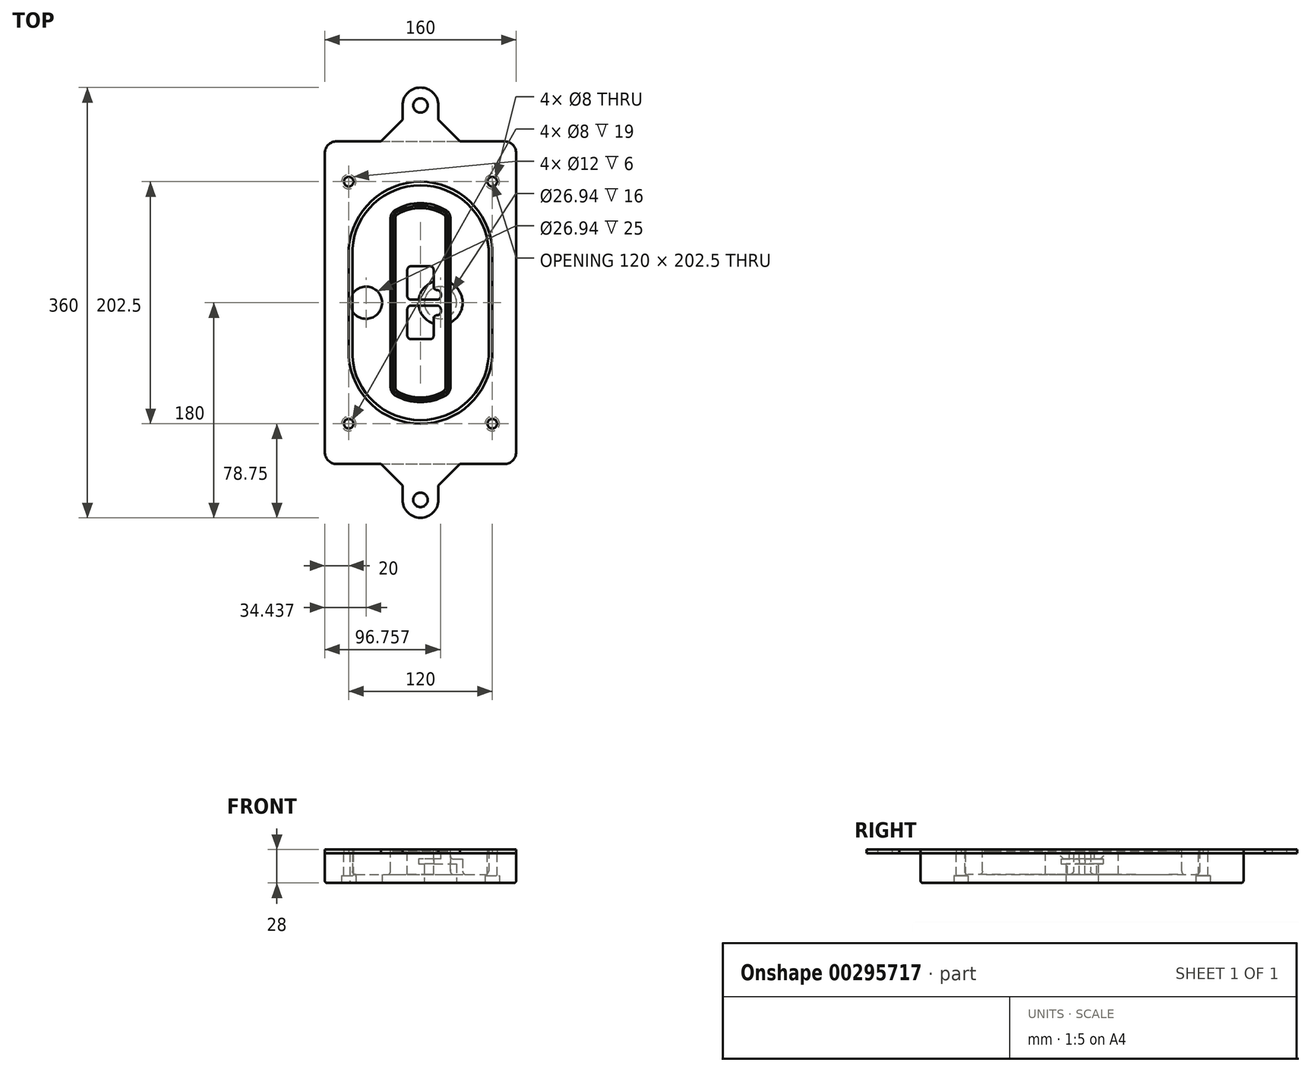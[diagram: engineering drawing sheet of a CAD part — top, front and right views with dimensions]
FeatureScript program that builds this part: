
annotation { "Feature Type Name" : "Feature", "Feature Type Description" : "" }
export const myFeature = defineFeature(function(context is Context, id is Id, definition is map)
    precondition{}
    {
        {
            var Q0;
            Q0=qCreatedBy(makeId("Top.planeOp"),FACE);
            var sketch = newSketch(context, id + "F0", { "sketchPlane" : qUnion([Q0])});
            skPoint(sketch, "E0.rect.middle", {"position": v(0, 0) * mm});
            skLineSegment(sketch, "E1.bottom", {"start": v(-70, -135) * mm, "end": v(70, -135) * mm});
            skLineSegment(sketch, "E1.top", {"start": v(-70, 135) * mm, "end": v(70, 135) * mm});
            skLineSegment(sketch, "E1.left", {"start": v(-80, -125) * mm, "end": v(-80, 125) * mm});
            skLineSegment(sketch, "E1.right", {"start": v(80, -125) * mm, "end": v(80, 125) * mm});
            skLineSegment(sketch, "E2", {"start": v(-80, 135) * mm, "end": v(80, -135) * mm, "construction": true});
            skLineSegment(sketch, "E3", {"start": v(80, 135) * mm, "end": v(-80, -135) * mm, "construction": true});
            skCircle(sketch, "E4", {"center": v(-60, 101.25) * mm, "radius": 4 * mm});
            skCircle(sketch, "E5", {"center": v(60, 101.25) * mm, "radius": 4 * mm});
            skCircle(sketch, "E6", {"center": v(60, -101.25) * mm, "radius": 4 * mm});
            skCircle(sketch, "E7", {"center": v(-60, -101.25) * mm, "radius": 4 * mm});
            skLineSegment(sketch, "E8", {"start": v(-60, 101.25) * mm, "end": v(60, 101.25) * mm, "construction": true});
            skLineSegment(sketch, "E9", {"start": v(60, 101.25) * mm, "end": v(60, -101.25) * mm, "construction": true});
            skLineSegment(sketch, "E10", {"start": v(60, -101.25) * mm, "end": v(-60, -101.25) * mm, "construction": true});
            skLineSegment(sketch, "E11", {"start": v(-60, -101.25) * mm, "end": v(-60, 101.25) * mm, "construction": true});
            skLineSegment(sketch, "E12", {"start": v(-60, 44.66) * mm, "end": v(-60, -44.66) * mm});
            skLineSegment(sketch, "E13", {"start": v(60, 44.66) * mm, "end": v(60, -44.66) * mm});
            skArc(sketch, "E14", {"start": v(59.98, 45.37) * mm, "mid": v(0, 101.25) * mm, "end": v(-59.98, 45.37) * mm});
            skArc(sketch, "E15", {"start": v(-59.98, -45.37) * mm, "mid": v(0, -101.25) * mm, "end": v(59.98, -45.37) * mm});
            skLineSegment(sketch, "E16", {"start": v(-60, 0) * mm, "end": v(60, 0) * mm, "construction": true});
            skPoint(sketch, "E17.visualSharp", {"position": v(-60, -45) * mm});
            skArc(sketch, "E17.filletArc", {"start": v(-60, -44.66) * mm, "mid": v(-60, -45.02) * mm, "end": v(-59.98, -45.37) * mm});
            skPoint(sketch, "E18.visualSharp", {"position": v(-60, 45) * mm});
            skArc(sketch, "E18.filletArc", {"start": v(-59.98, 45.37) * mm, "mid": v(-60, 45.02) * mm, "end": v(-60, 44.66) * mm});
            skPoint(sketch, "E19.visualSharp", {"position": v(60, 45) * mm});
            skArc(sketch, "E19.filletArc", {"start": v(60, 44.66) * mm, "mid": v(60, 45.02) * mm, "end": v(59.98, 45.37) * mm});
            skPoint(sketch, "E20.visualSharp", {"position": v(60, -45) * mm});
            skArc(sketch, "E20.filletArc", {"start": v(59.98, -45.37) * mm, "mid": v(60, -45.02) * mm, "end": v(60, -44.66) * mm});
            skPoint(sketch, "E21.visualSharp", {"position": v(-80, 135) * mm});
            skArc(sketch, "E21.filletArc", {"start": v(-70, 135) * mm, "mid": v(-77.07, 132.07) * mm, "end": v(-80, 125) * mm});
            skPoint(sketch, "E22.visualSharp", {"position": v(80, 135) * mm});
            skArc(sketch, "E22.filletArc", {"start": v(80, 125) * mm, "mid": v(77.07, 132.07) * mm, "end": v(70, 135) * mm});
            skPoint(sketch, "E23.visualSharp", {"position": v(80, -135) * mm});
            skArc(sketch, "E23.filletArc", {"start": v(70, -135) * mm, "mid": v(77.07, -132.07) * mm, "end": v(80, -125) * mm});
            skPoint(sketch, "E24.visualSharp", {"position": v(-80, -135) * mm});
            skArc(sketch, "E24.filletArc", {"start": v(-80, -125) * mm, "mid": v(-77.07, -132.07) * mm, "end": v(-70, -135) * mm});
            skArc(sketch, "E25.0", {"start": v(57, 44.66) * mm, "mid": v(57, 44.9) * mm, "end": v(56.98, 45.16) * mm});
            skLineSegment(sketch, "E25.1", {"start": v(57, 44.66) * mm, "end": v(57, -44.66) * mm});
            skArc(sketch, "E25.2", {"start": v(56.98, -45.16) * mm, "mid": v(57, -44.9) * mm, "end": v(57, -44.66) * mm});
            skArc(sketch, "E25.3", {"start": v(-56.98, -45.16) * mm, "mid": v(0, -98.25) * mm, "end": v(56.98, -45.16) * mm});
            skArc(sketch, "E25.4", {"start": v(-57, -44.66) * mm, "mid": v(-57, -44.9) * mm, "end": v(-56.98, -45.16) * mm});
            skArc(sketch, "E25.5", {"start": v(56.98, 45.16) * mm, "mid": v(0, 98.25) * mm, "end": v(-56.98, 45.16) * mm});
            skLineSegment(sketch, "E25.6", {"start": v(-57, 44.66) * mm, "end": v(-57, -44.66) * mm});
            skArc(sketch, "E25.7", {"start": v(-56.98, 45.16) * mm, "mid": v(-57, 44.9) * mm, "end": v(-57, 44.66) * mm});
            skArc(sketch, "E26.0", {"start": v(-63.97, 45.65) * mm, "mid": v(-64, 45.16) * mm, "end": v(-64, 44.66) * mm});
            skArc(sketch, "E26.1", {"start": v(63.97, 45.65) * mm, "mid": v(0, 105.25) * mm, "end": v(-63.97, 45.65) * mm});
            skArc(sketch, "E26.2", {"start": v(64, 44.66) * mm, "mid": v(64, 45.16) * mm, "end": v(63.97, 45.65) * mm});
            skLineSegment(sketch, "E26.3", {"start": v(64, 44.66) * mm, "end": v(64, -44.66) * mm});
            skArc(sketch, "E26.4", {"start": v(63.97, -45.65) * mm, "mid": v(64, -45.16) * mm, "end": v(64, -44.66) * mm});
            skLineSegment(sketch, "E26.5", {"start": v(-64, 44.66) * mm, "end": v(-64, -44.66) * mm});
            skArc(sketch, "E26.6", {"start": v(-63.97, -45.65) * mm, "mid": v(0, -105.25) * mm, "end": v(63.97, -45.65) * mm});
            skArc(sketch, "E26.7", {"start": v(-64, -44.66) * mm, "mid": v(-64, -45.16) * mm, "end": v(-63.97, -45.65) * mm});
            skSolve(sketch);
        }
        {
            var Q0;
            Q0=makeQuery(id+"F0.imprint","IMPRINT",FACE,{"disambiguationData":[TD([[makeQuery(id+"F0.imprint","IMPRINT",EDGE,{"derivedFrom":sQuery(id+"F0.wireOp",EDGE,"E1.bottom")}),1.0]])]});
            var Q1;
            Q1=makeQuery(id+"F0.imprint","IMPRINT",FACE,{"disambiguationData":[TD([[makeQuery(id+"F0.imprint","IMPRINT",EDGE,{"derivedFrom":sQuery(id+"F0.wireOp",EDGE,"E12")}),1.0]])]});
            var Q2;
            Q2=makeQuery(id+"F0.imprint","IMPRINT",FACE,{"disambiguationData":[TD([[makeQuery(id+"F0.imprint","IMPRINT",EDGE,{"derivedFrom":sQuery(id+"F0.wireOp",EDGE,"E25.0")}),1.0]])]});
            var Q3;
            Q3=makeQuery(id+"F0.imprint","IMPRINT",FACE,{"disambiguationData":[TD([[makeQuery(id+"F0.imprint","IMPRINT",EDGE,{"derivedFrom":sQuery(id+"F0.wireOp",EDGE,"E12")}),-1.0]])]});
            extrude(context, id + "F1", {"entities" : qUnion([Q0, Q1, Q2, Q3]), "oppositeDirection" : true, "depth" : 25 * mm});
        }
        {
            var Q0;
            Q0=makeQuery(id+"F0.imprint","IMPRINT",FACE,{"disambiguationData":[TD([[makeQuery(id+"F0.imprint","IMPRINT",EDGE,{"derivedFrom":sQuery(id+"F0.wireOp",EDGE,"E12")}),1.0]])]});
            extrude(context, id + "F2", {"entities" : qUnion([Q0]), "operationType" : NewBodyOperationType.ADD, "depth" : 3 * mm});
        }
        {
            var Q0;
            Q0=makeQuery(id+"F0.imprint","IMPRINT",FACE,{"disambiguationData":[TD([[makeQuery(id+"F0.imprint","IMPRINT",EDGE,{"derivedFrom":sQuery(id+"F0.wireOp",EDGE,"E25.0")}),1.0]])]});
            extrude(context, id + "F3", {"entities" : qUnion([Q0]), "operationType" : NewBodyOperationType.REMOVE, "oppositeDirection" : true, "depth" : 18 * mm});
        }
        {
            var Q0;
            Q0=makeQuery(id+"F2.opExtrude","CAP_FACE",FACE,{"disambiguationData":[OSD([sQuery(id+"F0.wireOp",EDGE,"E12"),sQuery(id+"F0.wireOp",EDGE,"E13"),sQuery(id+"F0.wireOp",EDGE,"E14"),sQuery(id+"F0.wireOp",EDGE,"E15"),sQuery(id+"F0.wireOp",EDGE,"E17.filletArc"),sQuery(id+"F0.wireOp",EDGE,"E18.filletArc"),sQuery(id+"F0.wireOp",EDGE,"E19.filletArc"),sQuery(id+"F0.wireOp",EDGE,"E20.filletArc"),sQuery(id+"F0.wireOp",EDGE,"E25.0"),sQuery(id+"F0.wireOp",EDGE,"E25.1"),sQuery(id+"F0.wireOp",EDGE,"E25.2"),sQuery(id+"F0.wireOp",EDGE,"E25.3"),sQuery(id+"F0.wireOp",EDGE,"E25.4"),sQuery(id+"F0.wireOp",EDGE,"E25.5"),sQuery(id+"F0.wireOp",EDGE,"E25.6"),sQuery(id+"F0.wireOp",EDGE,"E25.7")])],"isStart":false});
            var sketch = newSketch(context, id + "F4", { "sketchPlane" : qUnion([Q0])});
            skArc(sketch, "E27.0", {"start": v(-20.99, -77.65) * mm, "mid": v(0, -83.25) * mm, "end": v(20.99, -77.65) * mm});
            skArc(sketch, "E28.0", {"start": v(20.99, 77.65) * mm, "mid": v(0, 83.25) * mm, "end": v(-20.99, 77.65) * mm});
            skLineSegment(sketch, "E29", {"start": v(-25, 70.71) * mm, "end": v(-25, -70.71) * mm});
            skLineSegment(sketch, "E30", {"start": v(25, 70.71) * mm, "end": v(25, -70.71) * mm});
            skLineSegment(sketch, "E31", {"start": v(-25, 75.03) * mm, "end": v(25, 75.03) * mm, "construction": true});
            skLineSegment(sketch, "E32", {"start": v(-25, -75.03) * mm, "end": v(25, -75.03) * mm, "construction": true});
            skPoint(sketch, "E33.visualSharp", {"position": v(-25, 75.03) * mm});
            skArc(sketch, "E33.filletArc", {"start": v(-20.99, 77.65) * mm, "mid": v(-23.92, 74.72) * mm, "end": v(-25, 70.71) * mm});
            skPoint(sketch, "E34.visualSharp", {"position": v(25, 75.03) * mm});
            skArc(sketch, "E34.filletArc", {"start": v(25, 70.71) * mm, "mid": v(23.92, 74.72) * mm, "end": v(20.99, 77.65) * mm});
            skPoint(sketch, "E35.visualSharp", {"position": v(25, -75.03) * mm});
            skArc(sketch, "E35.filletArc", {"start": v(20.99, -77.65) * mm, "mid": v(23.92, -74.72) * mm, "end": v(25, -70.71) * mm});
            skPoint(sketch, "E36.visualSharp", {"position": v(-25, -75.03) * mm});
            skArc(sketch, "E36.filletArc", {"start": v(-25, -70.71) * mm, "mid": v(-23.92, -74.72) * mm, "end": v(-20.99, -77.65) * mm});
            skArc(sketch, "E37.0", {"start": v(56.98, 45.16) * mm, "mid": v(0, 98.25) * mm, "end": v(-56.98, 45.16) * mm});
            skArc(sketch, "E37.1", {"start": v(-56.98, 45.16) * mm, "mid": v(-57, 44.9) * mm, "end": v(-57, 44.66) * mm});
            skLineSegment(sketch, "E37.2", {"start": v(-57, 44.66) * mm, "end": v(-57, -44.66) * mm});
            skArc(sketch, "E37.3", {"start": v(-57, -44.66) * mm, "mid": v(-57, -44.9) * mm, "end": v(-56.98, -45.16) * mm});
            skArc(sketch, "E37.4", {"start": v(-56.98, -45.16) * mm, "mid": v(0, -98.25) * mm, "end": v(56.98, -45.16) * mm});
            skArc(sketch, "E37.5", {"start": v(56.98, -45.16) * mm, "mid": v(57, -44.9) * mm, "end": v(57, -44.66) * mm});
            skLineSegment(sketch, "E37.6", {"start": v(57, 44.66) * mm, "end": v(57, -44.66) * mm});
            skArc(sketch, "E37.7", {"start": v(57, 44.66) * mm, "mid": v(57, 44.9) * mm, "end": v(56.98, 45.16) * mm});
            skLineSegment(sketch, "E38.0", {"start": v(23, 70.71) * mm, "end": v(23, -70.71) * mm});
            skArc(sketch, "E38.1", {"start": v(19.99, -75.92) * mm, "mid": v(22.2, -73.72) * mm, "end": v(23, -70.71) * mm});
            skArc(sketch, "E38.2", {"start": v(-19.99, -75.92) * mm, "mid": v(0, -81.25) * mm, "end": v(19.99, -75.92) * mm});
            skArc(sketch, "E38.3", {"start": v(-23, -70.71) * mm, "mid": v(-22.2, -73.72) * mm, "end": v(-19.99, -75.92) * mm});
            skLineSegment(sketch, "E38.4", {"start": v(-23, 70.71) * mm, "end": v(-23, -70.71) * mm});
            skArc(sketch, "E38.5", {"start": v(23, 70.71) * mm, "mid": v(22.2, 73.72) * mm, "end": v(19.99, 75.92) * mm});
            skArc(sketch, "E38.6", {"start": v(-19.99, 75.92) * mm, "mid": v(-22.2, 73.72) * mm, "end": v(-23, 70.71) * mm});
            skArc(sketch, "E38.7", {"start": v(19.99, 75.92) * mm, "mid": v(0, 81.25) * mm, "end": v(-19.99, 75.92) * mm});
            skArc(sketch, "E39.0", {"start": v(21, 70.71) * mm, "mid": v(20.46, 72.72) * mm, "end": v(19, 74.18) * mm});
            skLineSegment(sketch, "E39.1", {"start": v(21, 70.71) * mm, "end": v(21, -70.71) * mm});
            skArc(sketch, "E39.2", {"start": v(19, -74.18) * mm, "mid": v(20.46, -72.72) * mm, "end": v(21, -70.71) * mm});
            skArc(sketch, "E39.3", {"start": v(-19, -74.18) * mm, "mid": v(0, -79.25) * mm, "end": v(19, -74.18) * mm});
            skArc(sketch, "E39.4", {"start": v(-21, -70.71) * mm, "mid": v(-20.46, -72.72) * mm, "end": v(-19, -74.18) * mm});
            skArc(sketch, "E39.5", {"start": v(19, 74.18) * mm, "mid": v(0, 79.25) * mm, "end": v(-19, 74.18) * mm});
            skLineSegment(sketch, "E39.6", {"start": v(-21, 70.71) * mm, "end": v(-21, -70.71) * mm});
            skArc(sketch, "E39.7", {"start": v(-19, 74.18) * mm, "mid": v(-20.46, 72.72) * mm, "end": v(-21, 70.71) * mm});
            skLineSegment(sketch, "E40", {"start": v(-25, 0) * mm, "end": v(25, 0) * mm, "construction": true});
            skLineSegment(sketch, "E41", {"start": v(-11, 5.5) * mm, "end": v(-11, 27.5) * mm});
            skLineSegment(sketch, "E42", {"start": v(-8, 30.5) * mm, "end": v(8, 30.5) * mm});
            skLineSegment(sketch, "E43", {"start": v(11, 27.5) * mm, "end": v(11, 13.5) * mm});
            skLineSegment(sketch, "E44", {"start": v(14, 10.5) * mm, "end": v(14, 10.5) * mm});
            skLineSegment(sketch, "E45", {"start": v(17, 7.5) * mm, "end": v(17, 5.5) * mm});
            skLineSegment(sketch, "E46", {"start": v(14, 2.5) * mm, "end": v(-8, 2.5) * mm});
            skPoint(sketch, "E47.visualSharp", {"position": v(-11, 30.5) * mm});
            skArc(sketch, "E47.filletArc", {"start": v(-8, 30.5) * mm, "mid": v(-10.12, 29.62) * mm, "end": v(-11, 27.5) * mm});
            skPoint(sketch, "E48.visualSharp", {"position": v(11, 30.5) * mm});
            skArc(sketch, "E48.filletArc", {"start": v(11, 27.5) * mm, "mid": v(10.12, 29.62) * mm, "end": v(8, 30.5) * mm});
            skPoint(sketch, "E49.visualSharp", {"position": v(11, 10.5) * mm});
            skArc(sketch, "E49.filletArc", {"start": v(11, 13.5) * mm, "mid": v(11.88, 11.38) * mm, "end": v(14, 10.5) * mm});
            skPoint(sketch, "E50.visualSharp", {"position": v(17, 10.5) * mm});
            skArc(sketch, "E50.filletArc", {"start": v(17, 7.5) * mm, "mid": v(16.12, 9.62) * mm, "end": v(14, 10.5) * mm});
            skPoint(sketch, "E51.visualSharp", {"position": v(17, 2.5) * mm});
            skArc(sketch, "E51.filletArc", {"start": v(14, 2.5) * mm, "mid": v(16.12, 3.38) * mm, "end": v(17, 5.5) * mm});
            skPoint(sketch, "E52.visualSharp", {"position": v(-11, 2.5) * mm});
            skArc(sketch, "E52.filletArc", {"start": v(-11, 5.5) * mm, "mid": v(-10.12, 3.38) * mm, "end": v(-8, 2.5) * mm});
            skLineSegment(sketch, "E53.0.MirrorCS", {"start": v(14, -2.5) * mm, "end": v(-8, -2.5) * mm});
            skArc(sketch, "E54.0.MirrorCS", {"start": v(-11, -5.5) * mm, "mid": v(-10.12, -3.38) * mm, "end": v(-8, -2.5) * mm});
            skLineSegment(sketch, "E55.0.MirrorCS", {"start": v(-11, -5.5) * mm, "end": v(-11, -27.5) * mm});
            skArc(sketch, "E56.0.MirrorCS", {"start": v(-8, -30.5) * mm, "mid": v(-10.12, -29.62) * mm, "end": v(-11, -27.5) * mm});
            skLineSegment(sketch, "E57.0.MirrorCS", {"start": v(-8, -30.5) * mm, "end": v(8, -30.5) * mm});
            skArc(sketch, "E58.0.MirrorCS", {"start": v(11, -27.5) * mm, "mid": v(10.12, -29.62) * mm, "end": v(8, -30.5) * mm});
            skLineSegment(sketch, "E59.0.MirrorCS", {"start": v(11, -27.5) * mm, "end": v(11, -13.5) * mm});
            skArc(sketch, "E60.0.MirrorCS", {"start": v(11, -13.5) * mm, "mid": v(11.88, -11.38) * mm, "end": v(14, -10.5) * mm});
            skArc(sketch, "E61.0.MirrorCS", {"start": v(17, -7.5) * mm, "mid": v(16.12, -9.62) * mm, "end": v(14, -10.5) * mm});
            skLineSegment(sketch, "E62.0.MirrorCS", {"start": v(17, -7.5) * mm, "end": v(17, -5.5) * mm});
            skArc(sketch, "E63.0.MirrorCS", {"start": v(14, -2.5) * mm, "mid": v(16.12, -3.38) * mm, "end": v(17, -5.5) * mm});
            skSolve(sketch);
        }
        {
            var Q0;
            Q0=makeQuery(id+"F4.imprint","IMPRINT",FACE,{"disambiguationData":[TD([[makeQuery(id+"F4.imprint","IMPRINT",EDGE,{"derivedFrom":sQuery(id+"F4.wireOp",EDGE,"E27.0")}),1.0]])]});
            var Q1;
            Q1=makeQuery(id+"F4.imprint","IMPRINT",FACE,{"disambiguationData":[TD([[makeQuery(id+"F4.imprint","IMPRINT",EDGE,{"derivedFrom":sQuery(id+"F4.wireOp",EDGE,"E38.0")}),-1.0]])]});
            var Q2;
            Q2=makeQuery(id+"F4.imprint","IMPRINT",FACE,{"disambiguationData":[TD([[makeQuery(id+"F4.imprint","IMPRINT",EDGE,{"derivedFrom":sQuery(id+"F4.wireOp",EDGE,"E39.0")}),1.0]])]});
            extrude(context, id + "F5", {"entities" : qUnion([Q0, Q1, Q2]), "operationType" : NewBodyOperationType.ADD, "endBound" : BoundingType.UP_TO_NEXT, "oppositeDirection" : true, "depth" : 25 * mm});
        }
        {
            var Q0;
            Q0=makeQuery(id+"F4.imprint","IMPRINT",FACE,{"disambiguationData":[TD([[makeQuery(id+"F4.imprint","IMPRINT",EDGE,{"derivedFrom":sQuery(id+"F4.wireOp",EDGE,"E38.0")}),-1.0]])]});
            extrude(context, id + "F6", {"entities" : qUnion([Q0]), "operationType" : NewBodyOperationType.REMOVE, "oppositeDirection" : true, "depth" : 2 * mm});
        }
        {
            var Q0;
            Q0=makeQuery(id+"F1.opExtrude","CAP_FACE",FACE,{"disambiguationData":[OSD([sQuery(id+"F0.wireOp",EDGE,"E1.bottom"),sQuery(id+"F0.wireOp",EDGE,"E1.top"),sQuery(id+"F0.wireOp",EDGE,"E1.left"),sQuery(id+"F0.wireOp",EDGE,"E1.right"),sQuery(id+"F0.wireOp",EDGE,"E4"),sQuery(id+"F0.wireOp",EDGE,"E5"),sQuery(id+"F0.wireOp",EDGE,"E6"),sQuery(id+"F0.wireOp",EDGE,"E7"),sQuery(id+"F0.wireOp",EDGE,"E21.filletArc"),sQuery(id+"F0.wireOp",EDGE,"E22.filletArc"),sQuery(id+"F0.wireOp",EDGE,"E23.filletArc"),sQuery(id+"F0.wireOp",EDGE,"E24.filletArc")])],"isStart":false});
            var sketch = newSketch(context, id + "F7", { "sketchPlane" : qUnion([Q0])});
            skCircle(sketch, "E64", {"center": v(16.76, 0) * mm, "radius": 13.47 * mm});
            skCircle(sketch, "E65", {"center": v(-45.56, 0) * mm, "radius": 13.47 * mm});
            skLineSegment(sketch, "E66", {"start": v(80, 0) * mm, "end": v(-80, 0) * mm});
            skCircle(sketch, "E67", {"center": v(16.76, 0) * mm, "radius": 18.47 * mm});
            skCircle(sketch, "E68", {"center": v(60, -101.25) * mm, "radius": 6 * mm});
            skCircle(sketch, "E69", {"center": v(-60, -101.25) * mm, "radius": 6 * mm});
            skCircle(sketch, "E70", {"center": v(-60, 101.25) * mm, "radius": 6 * mm});
            skCircle(sketch, "E71", {"center": v(60, 101.25) * mm, "radius": 6 * mm});
            skSolve(sketch);
        }
        {
            var Q0;
            {var subQ1=sQuery(id+"F7.wireOp",EDGE,"E66");var subQ4=sQuery(id+"F7.wireOp",EDGE,"E64");var subQ6=makeQuery(id+"F7.imprint","INTERSECT",VERTEX,{"disambiguationData":[OD(0.0)],"derivedFrom":[subQ4,subQ1]});Q0=makeQuery(id+"F7.imprint","IMPRINT",FACE,{"disambiguationData":[TD([[makeQuery(id+"F7.imprint","IMPRINT",EDGE,{"disambiguationData":[TD([[subQ6,-1.0]])],"derivedFrom":subQ4}),-1.0]])]});}
            var Q1;
            {var subQ0=sQuery(id+"F7.wireOp",EDGE,"E66");var subQ1=sQuery(id+"F7.wireOp",EDGE,"E64");var subQ3=makeQuery(id+"F7.imprint","INTERSECT",VERTEX,{"disambiguationData":[OD(0.0)],"derivedFrom":[subQ1,subQ0]});Q1=makeQuery(id+"F7.imprint","IMPRINT",FACE,{"disambiguationData":[TD([[makeQuery(id+"F7.imprint","IMPRINT",EDGE,{"disambiguationData":[TD([[subQ3,-1.0]])],"derivedFrom":subQ1}),1.0]])]});}
            var Q2;
            {var subQ0=sQuery(id+"F7.wireOp",EDGE,"E66");var subQ1=sQuery(id+"F7.wireOp",EDGE,"E64");var subQ3=makeQuery(id+"F7.imprint","INTERSECT",VERTEX,{"disambiguationData":[OD(0.0)],"derivedFrom":[subQ1,subQ0]});Q2=makeQuery(id+"F7.imprint","IMPRINT",FACE,{"disambiguationData":[TD([[makeQuery(id+"F7.imprint","IMPRINT",EDGE,{"disambiguationData":[TD([[subQ3,1.0]])],"derivedFrom":subQ1}),1.0]])]});}
            var Q3;
            {var subQ1=sQuery(id+"F7.wireOp",EDGE,"E66");var subQ4=sQuery(id+"F7.wireOp",EDGE,"E64");var subQ6=makeQuery(id+"F7.imprint","INTERSECT",VERTEX,{"disambiguationData":[OD(0.0)],"derivedFrom":[subQ4,subQ1]});Q3=makeQuery(id+"F7.imprint","IMPRINT",FACE,{"disambiguationData":[TD([[makeQuery(id+"F7.imprint","IMPRINT",EDGE,{"disambiguationData":[TD([[subQ6,1.0]])],"derivedFrom":subQ4}),-1.0]])]});}
            extrude(context, id + "F8", {"entities" : qUnion([Q0, Q1, Q2, Q3]), "operationType" : NewBodyOperationType.ADD, "oppositeDirection" : true, "depth" : 20 * mm});
        }
        {
            var Q0;
            {var subQ0=sQuery(id+"F7.wireOp",EDGE,"E66");var subQ1=sQuery(id+"F7.wireOp",EDGE,"E64");var subQ3=makeQuery(id+"F7.imprint","INTERSECT",VERTEX,{"disambiguationData":[OD(0.0)],"derivedFrom":[subQ1,subQ0]});Q0=makeQuery(id+"F7.imprint","IMPRINT",FACE,{"disambiguationData":[TD([[makeQuery(id+"F7.imprint","IMPRINT",EDGE,{"disambiguationData":[TD([[subQ3,-1.0]])],"derivedFrom":subQ1}),1.0]])]});}
            var Q1;
            {var subQ0=sQuery(id+"F7.wireOp",EDGE,"E66");var subQ1=sQuery(id+"F7.wireOp",EDGE,"E64");var subQ3=makeQuery(id+"F7.imprint","INTERSECT",VERTEX,{"disambiguationData":[OD(0.0)],"derivedFrom":[subQ1,subQ0]});Q1=makeQuery(id+"F7.imprint","IMPRINT",FACE,{"disambiguationData":[TD([[makeQuery(id+"F7.imprint","IMPRINT",EDGE,{"disambiguationData":[TD([[subQ3,1.0]])],"derivedFrom":subQ1}),1.0]])]});}
            extrude(context, id + "F9", {"entities" : qUnion([Q0, Q1]), "operationType" : NewBodyOperationType.REMOVE, "oppositeDirection" : true, "depth" : 16 * mm});
        }
        {
            var Q0;
            {var subQ0=sQuery(id+"F7.wireOp",EDGE,"E66");var subQ1=sQuery(id+"F7.wireOp",EDGE,"E65");var subQ3=makeQuery(id+"F7.imprint","INTERSECT",VERTEX,{"disambiguationData":[OD(0.0)],"derivedFrom":[subQ1,subQ0]});Q0=makeQuery(id+"F7.imprint","IMPRINT",FACE,{"disambiguationData":[TD([[makeQuery(id+"F7.imprint","IMPRINT",EDGE,{"disambiguationData":[TD([[subQ3,-1.0]])],"derivedFrom":subQ1}),1.0]])]});}
            var Q1;
            {var subQ0=sQuery(id+"F7.wireOp",EDGE,"E66");var subQ1=sQuery(id+"F7.wireOp",EDGE,"E65");var subQ3=makeQuery(id+"F7.imprint","INTERSECT",VERTEX,{"disambiguationData":[OD(0.0)],"derivedFrom":[subQ1,subQ0]});Q1=makeQuery(id+"F7.imprint","IMPRINT",FACE,{"disambiguationData":[TD([[makeQuery(id+"F7.imprint","IMPRINT",EDGE,{"disambiguationData":[TD([[subQ3,1.0]])],"derivedFrom":subQ1}),1.0]])]});}
            extrude(context, id + "F10", {"entities" : qUnion([Q0, Q1]), "operationType" : NewBodyOperationType.REMOVE, "oppositeDirection" : true, "depth" : 25 * mm});
        }
        {
            var Q0;
            Q0=makeQuery(id+"F7.imprint","IMPRINT",FACE,{"disambiguationData":[TD([[makeQuery(id+"F7.imprint","IMPRINT",EDGE,{"derivedFrom":sQuery(id+"F7.wireOp",EDGE,"E68")}),1.0]])]});
            var Q1;
            Q1=makeQuery(id+"F7.imprint","IMPRINT",FACE,{"disambiguationData":[TD([[makeQuery(id+"F7.imprint","IMPRINT",EDGE,{"derivedFrom":makeQuery(id+"F1.opExtrude","CAP_EDGE",EDGE,{"disambiguationData":[OSD([sQuery(id+"F0.wireOp",EDGE,"E5")])],"isStart":false})}),-1.0]])]});
            var Q2;
            Q2=makeQuery(id+"F7.imprint","IMPRINT",FACE,{"disambiguationData":[TD([[makeQuery(id+"F7.imprint","IMPRINT",EDGE,{"derivedFrom":sQuery(id+"F7.wireOp",EDGE,"E69")}),1.0]])]});
            var Q3;
            Q3=makeQuery(id+"F7.imprint","IMPRINT",FACE,{"disambiguationData":[TD([[makeQuery(id+"F7.imprint","IMPRINT",EDGE,{"derivedFrom":makeQuery(id+"F1.opExtrude","CAP_EDGE",EDGE,{"disambiguationData":[OSD([sQuery(id+"F0.wireOp",EDGE,"E4")])],"isStart":false})}),-1.0]])]});
            var Q4;
            Q4=makeQuery(id+"F7.imprint","IMPRINT",FACE,{"disambiguationData":[TD([[makeQuery(id+"F7.imprint","IMPRINT",EDGE,{"derivedFrom":sQuery(id+"F7.wireOp",EDGE,"E70")}),1.0]])]});
            var Q5;
            Q5=makeQuery(id+"F7.imprint","IMPRINT",FACE,{"disambiguationData":[TD([[makeQuery(id+"F7.imprint","IMPRINT",EDGE,{"derivedFrom":makeQuery(id+"F1.opExtrude","CAP_EDGE",EDGE,{"disambiguationData":[OSD([sQuery(id+"F0.wireOp",EDGE,"E7")])],"isStart":false})}),-1.0]])]});
            var Q6;
            Q6=makeQuery(id+"F7.imprint","IMPRINT",FACE,{"disambiguationData":[TD([[makeQuery(id+"F7.imprint","IMPRINT",EDGE,{"derivedFrom":sQuery(id+"F7.wireOp",EDGE,"E71")}),1.0]])]});
            var Q7;
            Q7=makeQuery(id+"F7.imprint","IMPRINT",FACE,{"disambiguationData":[TD([[makeQuery(id+"F7.imprint","IMPRINT",EDGE,{"derivedFrom":makeQuery(id+"F1.opExtrude","CAP_EDGE",EDGE,{"disambiguationData":[OSD([sQuery(id+"F0.wireOp",EDGE,"E6")])],"isStart":false})}),-1.0]])]});
            extrude(context, id + "F11", {"entities" : qUnion([Q0, Q1, Q2, Q3, Q4, Q5, Q6, Q7]), "operationType" : NewBodyOperationType.REMOVE, "oppositeDirection" : true, "depth" : 6 * mm});
        }
        {
            var Q0;
            Q0=makeQuery(id+"F9.boolean.opBoolean","COPY",FACE,{"derivedFrom":makeQuery(id+"F9.opExtrude","CAP_FACE",FACE,{"disambiguationData":[OSD([sQuery(id+"F7.wireOp",EDGE,"E64")])],"isStart":false})});
            var sketch = newSketch(context, id + "F12", { "sketchPlane" : qUnion([Q0])});
            skArc(sketch, "E72.0", {"start": v(11, 17.55) * mm, "mid": v(2.57, 11.82) * mm, "end": v(-1.54, 2.5) * mm});
            skArc(sketch, "E72.1", {"start": v(-1.54, -2.5) * mm, "mid": v(2.57, -11.82) * mm, "end": v(11, -17.55) * mm});
            skLineSegment(sketch, "E73", {"start": v(-1.54, -2.5) * mm, "end": v(14, -2.5) * mm});
            skLineSegment(sketch, "E74.0", {"start": v(14, 2.5) * mm, "end": v(-1.54, 2.5) * mm});
            skArc(sketch, "E74.1", {"start": v(14, 2.5) * mm, "mid": v(16.12, 3.38) * mm, "end": v(17, 5.5) * mm});
            skLineSegment(sketch, "E74.2", {"start": v(17, 7.5) * mm, "end": v(17, 5.5) * mm});
            skArc(sketch, "E74.3", {"start": v(17, 7.5) * mm, "mid": v(16.12, 9.62) * mm, "end": v(14, 10.5) * mm});
            skArc(sketch, "E74.4", {"start": v(11, 13.5) * mm, "mid": v(11.88, 11.38) * mm, "end": v(14, 10.5) * mm});
            skLineSegment(sketch, "E74.5", {"start": v(11, 17.55) * mm, "end": v(11, 13.5) * mm});
            skLineSegment(sketch, "E74.7", {"start": v(14, -2.5) * mm, "end": v(-1.54, -2.5) * mm});
            skArc(sketch, "E74.8", {"start": v(14, -2.5) * mm, "mid": v(16.12, -3.38) * mm, "end": v(17, -5.5) * mm});
            skLineSegment(sketch, "E74.9", {"start": v(17, -7.5) * mm, "end": v(17, -5.5) * mm});
            skArc(sketch, "E74.10", {"start": v(17, -7.5) * mm, "mid": v(16.12, -9.62) * mm, "end": v(14, -10.5) * mm});
            skArc(sketch, "E74.11", {"start": v(11, -13.5) * mm, "mid": v(11.88, -11.38) * mm, "end": v(14, -10.5) * mm});
            skLineSegment(sketch, "E74.12", {"start": v(11, -17.55) * mm, "end": v(11, -13.5) * mm});
            skPoint(sketch, "E75.orphan", {"position": v(11, -27.5) * mm});
            skPoint(sketch, "E76.orphan", {"position": v(-8, -2.5) * mm});
            skPoint(sketch, "E77.orphan", {"position": v(-8, 2.5) * mm});
            skPoint(sketch, "E78.orphan", {"position": v(11, 27.5) * mm});
            skSolve(sketch);
        }
        {
            var Q0;
            {var subQ7=sQuery(id+"F12.wireOp",EDGE,"E72.0");var subQ14=sQuery(id+"F12.wireOp",EDGE,"E72.1");var subQ16=sQuery(id+"F12.wireOp",EDGE,"E74.1");var subQ18=sQuery(id+"F12.wireOp",EDGE,"E74.8");Q0=qUnion([makeQuery(id+"F12.imprint","IMPRINT",FACE,{"disambiguationData":[TD([[makeQuery(id+"F12.imprint","IMPRINT",EDGE,{"derivedFrom":subQ7}),1.0]])]}),makeQuery(id+"F12.imprint","IMPRINT",FACE,{"disambiguationData":[TD([[makeQuery(id+"F12.imprint","IMPRINT",EDGE,{"derivedFrom":subQ14}),1.0]])]}),makeQuery(id+"F12.imprint","IMPRINT",FACE,{"disambiguationData":[TD([[makeQuery(id+"F12.imprint","IMPRINT",EDGE,{"derivedFrom":subQ16}),1.0]])]}),makeQuery(id+"F12.imprint","IMPRINT",FACE,{"disambiguationData":[TD([[makeQuery(id+"F12.imprint","IMPRINT",EDGE,{"derivedFrom":subQ18}),-1.0]])]})]);}
            var Q1;
            Q1=makeQuery(id+"F5.boolean.opBoolean","SPLIT",FACE,{"disambiguationData":[TD([makeQuery(id+"F5.opExtrude","SWEPT_FACE",FACE,{"disambiguationData":[OSD([sQuery(id+"F4.wireOp",EDGE,"E41")])]})])],"derivedFrom":makeQuery(id+"F3.boolean.opBoolean","COPY",FACE,{"derivedFrom":makeQuery(id+"F3.opExtrude","CAP_FACE",FACE,{"disambiguationData":[OSD([sQuery(id+"F0.wireOp",EDGE,"E25.0"),sQuery(id+"F0.wireOp",EDGE,"E25.1"),sQuery(id+"F0.wireOp",EDGE,"E25.2"),sQuery(id+"F0.wireOp",EDGE,"E25.3"),sQuery(id+"F0.wireOp",EDGE,"E25.4"),sQuery(id+"F0.wireOp",EDGE,"E25.5"),sQuery(id+"F0.wireOp",EDGE,"E25.6"),sQuery(id+"F0.wireOp",EDGE,"E25.7")])],"isStart":false})})});
            extrude(context, id + "F13", {"entities" : qUnion([Q0]), "operationType" : NewBodyOperationType.REMOVE, "endBound" : BoundingType.UP_TO_SURFACE, "endBoundEntityFace" : qUnion([Q1]), "depth" : 25 * mm});
        }
        {
            var Q0;
            Q0=makeQuery(id+"F3.boolean.opBoolean","COPY",EDGE,{"derivedFrom":makeQuery(id+"F3.opExtrude","CAP_EDGE",EDGE,{"disambiguationData":[OSD([sQuery(id+"F0.wireOp",EDGE,"E25.6")])],"isStart":false})});
            var Q1;
            Q1=makeQuery(id+"F8.boolean.opBoolean","INTERSECT",EDGE,{"derivedFrom":[makeQuery(id+"F5.opExtrude","SWEPT_FACE",FACE,{"disambiguationData":[OSD([sQuery(id+"F4.wireOp",EDGE,"E30")])]}),makeQuery(id+"F8.opExtrude","CAP_FACE",FACE,{"disambiguationData":[OSD([sQuery(id+"F7.wireOp",EDGE,"E67")])],"isStart":false})]});
            var Q2;
            Q2=makeQuery(id+"F8.boolean.opBoolean","INTERSECT",EDGE,{"disambiguationData":[OD(1.0)],"derivedFrom":[makeQuery(id+"F5.opExtrude","SWEPT_FACE",FACE,{"disambiguationData":[OSD([sQuery(id+"F4.wireOp",EDGE,"E30")])]}),makeQuery(id+"F8.opExtrude","SWEPT_FACE",FACE,{"disambiguationData":[OSD([sQuery(id+"F7.wireOp",EDGE,"E67")])]})]});
            var Q3;
            {var subQ0=sQuery(id+"F4.wireOp",EDGE,"E30");Q3=makeQuery(id+"F8.boolean.opBoolean","SPLIT",EDGE,{"disambiguationData":[TD([makeQuery(id+"F5.opExtrude","SWEPT_FACE",FACE,{"disambiguationData":[OSD([sQuery(id+"F4.wireOp",EDGE,"E35.filletArc")])]})])],"derivedFrom":makeQuery(id+"F5.opExtrude","CAP_EDGE",EDGE,{"disambiguationData":[OSD([subQ0])],"isStart":false})});}
            var Q4;
            {var subQ0=sQuery(id+"F0.wireOp",EDGE,"E25.7");var subQ1=sQuery(id+"F0.wireOp",EDGE,"E25.1");var subQ2=sQuery(id+"F0.wireOp",EDGE,"E25.6");var subQ3=sQuery(id+"F0.wireOp",EDGE,"E25.5");var subQ4=sQuery(id+"F0.wireOp",EDGE,"E25.4");var subQ5=sQuery(id+"F0.wireOp",EDGE,"E25.0");var subQ6=sQuery(id+"F0.wireOp",EDGE,"E25.2");var subQ7=sQuery(id+"F0.wireOp",EDGE,"E25.3");Q4=makeQuery(id+"F8.boolean.opBoolean","INTERSECT",EDGE,{"derivedFrom":[makeQuery(id+"F5.boolean.opBoolean","SPLIT",FACE,{"disambiguationData":[TD([makeQuery(id+"F2.opExtrude","SWEPT_FACE",FACE,{"disambiguationData":[OSD([subQ5])]})])],"derivedFrom":makeQuery(id+"F3.boolean.opBoolean","COPY",FACE,{"derivedFrom":makeQuery(id+"F3.opExtrude","CAP_FACE",FACE,{"disambiguationData":[OSD([subQ5,subQ1,subQ6,subQ7,subQ4,subQ3,subQ2,subQ0])],"isStart":false})})}),makeQuery(id+"F8.opExtrude","SWEPT_FACE",FACE,{"disambiguationData":[OSD([sQuery(id+"F7.wireOp",EDGE,"E67")])]})]});}
            var Q5;
            Q5=makeQuery(id+"F8.boolean.opBoolean","INTERSECT",EDGE,{"disambiguationData":[OD(0.0)],"derivedFrom":[makeQuery(id+"F5.opExtrude","SWEPT_FACE",FACE,{"disambiguationData":[OSD([sQuery(id+"F4.wireOp",EDGE,"E30")])]}),makeQuery(id+"F8.opExtrude","SWEPT_FACE",FACE,{"disambiguationData":[OSD([sQuery(id+"F7.wireOp",EDGE,"E67")])]})]});
            fillet(context, id + "F14", {"entities" : qUnion([Q0, Q1, Q2, Q3, Q4, Q5]), "radius" : 3 * mm, "tangentPropagation" : true, "allowEdgeOverflow" : false});
        }
        {
            var Q0;
            Q0=makeQuery(id+"F1.opExtrude","CAP_EDGE",EDGE,{"disambiguationData":[OSD([sQuery(id+"F0.wireOp",EDGE,"E1.bottom")])],"isStart":false});
            fillet(context, id + "F15", {"entities" : qUnion([Q0]), "radius" : 2 * mm, "tangentPropagation" : true, "allowEdgeOverflow" : false});
        }
        {
            var Q0;
            {var subQ0=sQuery(id+"F0.wireOp",EDGE,"E21.filletArc");var subQ1=sQuery(id+"F0.wireOp",EDGE,"E7");var subQ2=sQuery(id+"F0.wireOp",EDGE,"E6");var subQ3=sQuery(id+"F0.wireOp",EDGE,"E5");var subQ4=sQuery(id+"F0.wireOp",EDGE,"E4");var subQ5=sQuery(id+"F0.wireOp",EDGE,"E22.filletArc");var subQ6=sQuery(id+"F0.wireOp",EDGE,"E1.bottom");var subQ7=sQuery(id+"F0.wireOp",EDGE,"E1.right");var subQ8=sQuery(id+"F0.wireOp",EDGE,"E1.top");var subQ9=sQuery(id+"F0.wireOp",EDGE,"E1.left");var subQ10=sQuery(id+"F0.wireOp",EDGE,"E23.filletArc");var subQ11=sQuery(id+"F0.wireOp",EDGE,"E24.filletArc");Q0=makeQuery(id+"F2.boolean.opBoolean","SPLIT",FACE,{"disambiguationData":[TD([makeQuery(id+"F1.opExtrude","SWEPT_FACE",FACE,{"disambiguationData":[OSD([subQ6])]})])],"derivedFrom":makeQuery(id+"F1.opExtrude","CAP_FACE",FACE,{"disambiguationData":[OSD([subQ6,subQ8,subQ9,subQ7,subQ4,subQ3,subQ2,subQ1,subQ0,subQ5,subQ10,subQ11])],"isStart":true})});}
            var sketch = newSketch(context, id + "F16", { "sketchPlane" : qUnion([Q0])});
            skLineSegment(sketch, "E79", {"start": v(0, 135) * mm, "end": v(0, 165) * mm, "construction": true});
            skCircle(sketch, "E80", {"center": v(0, 165) * mm, "radius": 6 * mm});
            skLineSegment(sketch, "E81", {"start": v(-15, 165) * mm, "end": v(-15, 153) * mm});
            skLineSegment(sketch, "E82", {"start": v(-15, 153) * mm, "end": v(-33, 135) * mm});
            skLineSegment(sketch, "E83.MirrorCS", {"start": v(15, 165) * mm, "end": v(15, 153) * mm});
            skLineSegment(sketch, "E84.MirrorCS", {"start": v(15, 153) * mm, "end": v(33, 135) * mm});
            skArc(sketch, "E85", {"start": v(15, 165) * mm, "mid": v(0, 180) * mm, "end": v(-15, 165) * mm});
            skLineSegment(sketch, "E86", {"start": v(-80, 0) * mm, "end": v(80, 0) * mm, "construction": true});
            skLineSegment(sketch, "E87.MirrorCS", {"start": v(15, -153) * mm, "end": v(33, -135) * mm});
            skLineSegment(sketch, "E88.MirrorCS", {"start": v(-15, -153) * mm, "end": v(-33, -135) * mm});
            skLineSegment(sketch, "E89.MirrorCS", {"start": v(-15, -165) * mm, "end": v(-15, -153) * mm});
            skArc(sketch, "E90.MirrorCS", {"start": v(15, -165) * mm, "mid": v(0, -180) * mm, "end": v(-15, -165) * mm});
            skCircle(sketch, "E91.MirrorC", {"center": v(0, -165) * mm, "radius": 6 * mm});
            skLineSegment(sketch, "E92.MirrorCS", {"start": v(15, -165) * mm, "end": v(15, -153) * mm});
            skLineSegment(sketch, "E93.MirrorCS", {"start": v(0, -135) * mm, "end": v(0, -165) * mm, "construction": true});
            skSolve(sketch);
        }
        {
            var Q0;
            Q0=makeQuery(id+"F16.imprint","IMPRINT",FACE,{"disambiguationData":[TD([[makeQuery(id+"F16.imprint","IMPRINT",EDGE,{"derivedFrom":sQuery(id+"F16.wireOp",EDGE,"E80")}),-1.0]])]});
            var Q1;
            {var subQ1=sQuery(id+"F16.wireOp",EDGE,"E87.MirrorCS");Q1=makeQuery(id+"F16.imprint","IMPRINT",FACE,{"disambiguationData":[TD([[makeQuery(id+"F16.imprint","IMPRINT",EDGE,{"derivedFrom":subQ1}),1.0]])]});}
            var Q2;
            Q2=makeQuery(id+"F16.imprint","IMPRINT",FACE,{"disambiguationData":[TD([[makeQuery(id+"F16.imprint","IMPRINT",EDGE,{"derivedFrom":makeQuery(id+"F1.opExtrude","CAP_EDGE",EDGE,{"disambiguationData":[OSD([sQuery(id+"F0.wireOp",EDGE,"E1.left")])],"isStart":true})}),-1.0]])]});
            var Q3;
            Q3=makeQuery(id+"F2.opExtrude","CAP_FACE",FACE,{"disambiguationData":[OSD([sQuery(id+"F0.wireOp",EDGE,"E12"),sQuery(id+"F0.wireOp",EDGE,"E13"),sQuery(id+"F0.wireOp",EDGE,"E14"),sQuery(id+"F0.wireOp",EDGE,"E15"),sQuery(id+"F0.wireOp",EDGE,"E17.filletArc"),sQuery(id+"F0.wireOp",EDGE,"E18.filletArc"),sQuery(id+"F0.wireOp",EDGE,"E19.filletArc"),sQuery(id+"F0.wireOp",EDGE,"E20.filletArc"),sQuery(id+"F0.wireOp",EDGE,"E25.0"),sQuery(id+"F0.wireOp",EDGE,"E25.1"),sQuery(id+"F0.wireOp",EDGE,"E25.2"),sQuery(id+"F0.wireOp",EDGE,"E25.3"),sQuery(id+"F0.wireOp",EDGE,"E25.4"),sQuery(id+"F0.wireOp",EDGE,"E25.5"),sQuery(id+"F0.wireOp",EDGE,"E25.6"),sQuery(id+"F0.wireOp",EDGE,"E25.7")])],"isStart":false});
            extrude(context, id + "F17", {"entities" : qUnion([Q0, Q1, Q2]), "endBound" : BoundingType.UP_TO_SURFACE, "endBoundEntityFace" : qUnion([Q3]), "depth" : 25 * mm});
        }
    });
